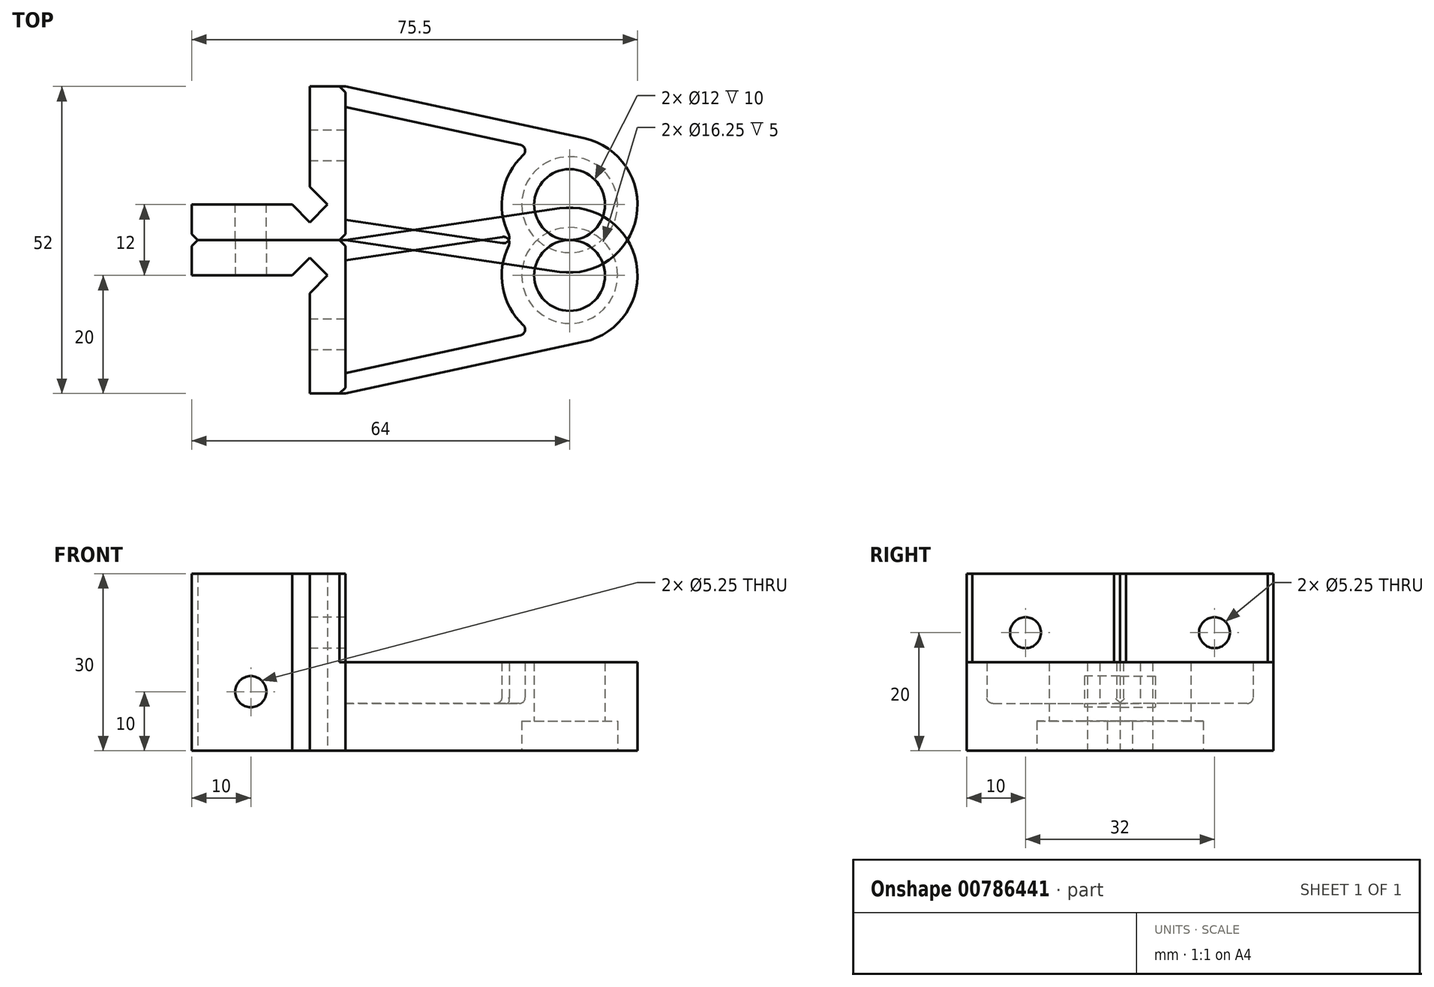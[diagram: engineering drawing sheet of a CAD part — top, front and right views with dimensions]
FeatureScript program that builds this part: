
annotation { "Feature Type Name" : "Feature", "Feature Type Description" : "" }
export const myFeature = defineFeature(function(context is Context, id is Id, definition is map)
    precondition{}
    {
        {
            var Q0;
            Q0=qCreatedBy(makeId("Top.planeOp"),FACE);
            var sketch = newSketch(context, id + "F0", { "sketchPlane" : qUnion([Q0])});
            skLineSegment(sketch, "E0", {"start": v(2.44, 11.24) * mm, "end": v(-38, 20) * mm, "construction": true});
            skLineSegment(sketch, "E1", {"start": v(-38, 20) * mm, "end": v(-44, 20) * mm, "construction": true});
            skLineSegment(sketch, "E2", {"start": v(-44, 20) * mm, "end": v(-44, 3) * mm, "construction": true});
            skLineSegment(sketch, "E3", {"start": v(-44, 3) * mm, "end": v(-41, 0) * mm, "construction": true});
            skLineSegment(sketch, "E4", {"start": v(-41, 0) * mm, "end": v(-44, -3) * mm, "construction": true});
            skLineSegment(sketch, "E5", {"start": v(-44, -3) * mm, "end": v(-47, 0) * mm, "construction": true});
            skLineSegment(sketch, "E6", {"start": v(-47, 0) * mm, "end": v(-64, 0) * mm, "construction": true});
            skLineSegment(sketch, "E7", {"start": v(-64, 0) * mm, "end": v(-64, -6) * mm, "construction": true});
            skLineSegment(sketch, "E8", {"start": v(-64, -6) * mm, "end": v(-38, -6) * mm, "construction": true});
            skLineSegment(sketch, "E9", {"start": v(-38, -6) * mm, "end": v(-1.68, -11.38) * mm, "construction": true});
            skCircle(sketch, "E10", {"center": v(0, 0) * mm, "radius": 6 * mm, "construction": true});
            skArc(sketch, "E11", {"start": v(2.44, 11.24) * mm, "mid": v(11.31, -2.06) * mm, "end": v(-1.68, -11.38) * mm, "construction": true});
            skLineSegment(sketch, "E12.0", {"start": v(1.72, 7.94) * mm, "end": v(-38, 16.55) * mm, "construction": true});
            skLineSegment(sketch, "E12.2", {"start": v(-38, -2.59) * mm, "end": v(-1.19, -8.04) * mm, "construction": true});
            skCircle(sketch, "E13.converted", {"center": v(0, 0) * mm, "radius": 8.12 * mm, "construction": true});
            skSolve(sketch);
        }
        {
            var Q0;
            Q0=qCreatedBy(makeId("Top.planeOp"),FACE);
            var sketch = newSketch(context, id + "F1", { "sketchPlane" : qUnion([Q0])});
            skLineSegment(sketch, "E14.0", {"start": v(2.44, 11.24) * mm, "end": v(-38, 20) * mm});
            skLineSegment(sketch, "E15.0", {"start": v(-38, -6) * mm, "end": v(-1.68, -11.38) * mm});
            skArc(sketch, "E16.0", {"start": v(2.44, 11.24) * mm, "mid": v(11.31, -2.06) * mm, "end": v(-1.68, -11.38) * mm});
            skCircle(sketch, "E17.0", {"center": v(0, 0) * mm, "radius": 6 * mm});
            skLineSegment(sketch, "E18", {"start": v(-38, 20) * mm, "end": v(-38, -6) * mm});
            skSolve(sketch);
        }
        {
            var Q0;
            Q0 = qSketchRegion(id + "F1", true);
            extrude(context, id + "F2", {"entities" : qUnion([Q0]), "depth" : 8 * mm, "offsetDistance" : 25 * mm});
        }
        {
            var Q0;
            Q0=qCreatedBy(makeId("Top.planeOp"),FACE);
            var sketch = newSketch(context, id + "F3", { "sketchPlane" : qUnion([Q0])});
            skLineSegment(sketch, "E19.0", {"start": v(-6.23, 9.66) * mm, "end": v(-38, 16.55) * mm});
            skLineSegment(sketch, "E20.0", {"start": v(-38, -2.59) * mm, "end": v(-9.24, -6.85) * mm});
            skLineSegment(sketch, "E21.0", {"start": v(2.44, 11.24) * mm, "end": v(-38, 20) * mm});
            skLineSegment(sketch, "E22.0", {"start": v(-38, -6) * mm, "end": v(-1.68, -11.38) * mm});
            skLineSegment(sketch, "E23", {"start": v(-38, 20) * mm, "end": v(-38, 16.55) * mm});
            skLineSegment(sketch, "E24", {"start": v(-38, -2.59) * mm, "end": v(-38, -6) * mm});
            skArc(sketch, "E25.converted", {"start": v(2.44, 11.24) * mm, "mid": v(11.31, -2.06) * mm, "end": v(-1.68, -11.38) * mm});
            skArc(sketch, "E26.trimOffspring", {"start": v(-9.24, -6.85) * mm, "mid": v(-11.31, 2.06) * mm, "end": v(-6.23, 9.66) * mm});
            skCircle(sketch, "E27.0", {"center": v(0, 0) * mm, "radius": 6 * mm});
            skSolve(sketch);
        }
        {
            var Q0;
            Q0 = qSketchRegion(id + "F3", true);
            extrude(context, id + "F4", {"entities" : qUnion([Q0]), "operationType" : NewBodyOperationType.ADD, "depth" : 15 * mm, "offsetDistance" : 25 * mm});
        }
        {
            var Q0;
            Q0=qCreatedBy(makeId("Top.planeOp"),FACE);
            var sketch = newSketch(context, id + "F5", { "sketchPlane" : qUnion([Q0])});
            skLineSegment(sketch, "E28.0", {"start": v(-38, 20) * mm, "end": v(-44, 20) * mm});
            skLineSegment(sketch, "E29.0", {"start": v(-44, 20) * mm, "end": v(-44, 3) * mm});
            skLineSegment(sketch, "E30.0", {"start": v(-44, 3) * mm, "end": v(-41, 0) * mm});
            skLineSegment(sketch, "E31.0", {"start": v(-41, 0) * mm, "end": v(-44, -3) * mm});
            skLineSegment(sketch, "E32.0", {"start": v(-44, -3) * mm, "end": v(-47, 0) * mm});
            skLineSegment(sketch, "E33.0", {"start": v(-47, 0) * mm, "end": v(-64, 0) * mm});
            skLineSegment(sketch, "E34.0", {"start": v(-64, 0) * mm, "end": v(-64, -6) * mm});
            skLineSegment(sketch, "E35.0", {"start": v(-64, -6) * mm, "end": v(-38, -6) * mm});
            skLineSegment(sketch, "E36", {"start": v(-38, 20) * mm, "end": v(-38, -6) * mm});
            skSolve(sketch);
        }
        {
            var Q0;
            Q0 = qSketchRegion(id + "F5", true);
            extrude(context, id + "F6", {"entities" : qUnion([Q0]), "operationType" : NewBodyOperationType.ADD, "depth" : 30 * mm, "offsetDistance" : 25 * mm});
        }
        {
            var Q0;
            Q0=makeQuery(id+"F6.opExtrude","SWEPT_EDGE",EDGE,{"disambiguationData":[OSD([sQuery(id+"F5.wireOp",EDGE,"E34.0"),sQuery(id+"F5.wireOp",EDGE,"E35.0")])]});
            var Q1;
            Q1=makeQuery(id+"F6.boolean.opBoolean","SPLIT",EDGE,{"derivedFrom":makeQuery(id+"F6.opExtrude","SWEPT_EDGE",EDGE,{"disambiguationData":[OSD([sQuery(id+"F5.wireOp",EDGE,"E28.0"),sQuery(id+"F5.wireOp",EDGE,"E36")])]})});
            var Q2;
            Q2=makeQuery(id+"F6.boolean.opBoolean","SPLIT",EDGE,{"derivedFrom":makeQuery(id+"F6.opExtrude","SWEPT_EDGE",EDGE,{"disambiguationData":[OSD([sQuery(id+"F5.wireOp",EDGE,"E35.0"),sQuery(id+"F5.wireOp",EDGE,"E36")])]})});
            chamfer(context, id + "F7", {"entities" : qUnion([Q0, Q1, Q2]), "width" : 1 * mm, "tangentPropagation" : true});
        }
        {
            var Q0;
            Q0=makeQuery(id+"F4.boolean.opBoolean","INTERSECT",EDGE,{"derivedFrom":[makeQuery(id+"F2.opExtrude","CAP_FACE",FACE,{"disambiguationData":[OSD([sQuery(id+"F1.wireOp",EDGE,"E14.0"),sQuery(id+"F1.wireOp",EDGE,"E15.0"),sQuery(id+"F1.wireOp",EDGE,"E16.0"),sQuery(id+"F1.wireOp",EDGE,"E17.0"),sQuery(id+"F1.wireOp",EDGE,"E18")])],"isStart":false}),makeQuery(id+"F4.opExtrude","SWEPT_FACE",FACE,{"disambiguationData":[OSD([sQuery(id+"F3.wireOp",EDGE,"E19.0")])]})]});
            var Q1;
            Q1=makeQuery(id+"F2.opExtrude","CAP_EDGE",EDGE,{"disambiguationData":[OSD([sQuery(id+"F1.wireOp",EDGE,"E18")])],"isStart":false});
            var Q2;
            Q2=makeQuery(id+"F4.opExtrude","CAP_EDGE",EDGE,{"disambiguationData":[OSD([sQuery(id+"F3.wireOp",EDGE,"E24")])],"isStart":false});
            var Q3;
            Q3=makeQuery(id+"F4.opExtrude","CAP_EDGE",EDGE,{"disambiguationData":[OSD([sQuery(id+"F3.wireOp",EDGE,"E23")])],"isStart":false});
            var Q4;
            Q4=makeQuery(id+"F4.boolean.opBoolean","INTERSECT",EDGE,{"derivedFrom":[makeQuery(id+"F2.opExtrude","CAP_FACE",FACE,{"disambiguationData":[OSD([sQuery(id+"F1.wireOp",EDGE,"E14.0"),sQuery(id+"F1.wireOp",EDGE,"E15.0"),sQuery(id+"F1.wireOp",EDGE,"E16.0"),sQuery(id+"F1.wireOp",EDGE,"E17.0"),sQuery(id+"F1.wireOp",EDGE,"E18")])],"isStart":false}),makeQuery(id+"F4.opExtrude","SWEPT_FACE",FACE,{"disambiguationData":[OSD([sQuery(id+"F3.wireOp",EDGE,"E26.trimOffspring")])]})]});
            var Q5;
            Q5=makeQuery(id+"F4.opExtrude","SWEPT_EDGE",EDGE,{"disambiguationData":[OSD([sQuery(id+"F3.wireOp",EDGE,"E19.0"),sQuery(id+"F3.wireOp",EDGE,"E26.trimOffspring")])]});
            var Q6;
            Q6=makeQuery(id+"F4.opExtrude","SWEPT_EDGE",EDGE,{"disambiguationData":[OSD([sQuery(id+"F3.wireOp",EDGE,"E20.0"),sQuery(id+"F3.wireOp",EDGE,"E26.trimOffspring")])]});
            var Q7;
            Q7=makeQuery(id+"F4.opExtrude","SWEPT_EDGE",EDGE,{"disambiguationData":[OSD([sQuery(id+"F3.wireOp",EDGE,"E19.0"),sQuery(id+"F3.wireOp",EDGE,"E23")])]});
            var Q8;
            Q8=makeQuery(id+"F4.opExtrude","SWEPT_EDGE",EDGE,{"disambiguationData":[OSD([sQuery(id+"F3.wireOp",EDGE,"E20.0"),sQuery(id+"F3.wireOp",EDGE,"E24")])]});
            fillet(context, id + "F8", {"entities" : qUnion([Q0, Q1, Q2, Q3, Q4, Q5, Q6, Q7, Q8]), "radius" : 1 * mm, "tangentPropagation" : true, "allowEdgeOverflow" : false});
        }
        {
            var Q0;
            Q0=makeQuery(id+"F6.boolean.opBoolean","MERGE",FACE,{"derivedFrom":[makeQuery(id+"F4.boolean.opBoolean","MERGE",FACE,{"derivedFrom":[makeQuery(id+"F2.opExtrude","CAP_FACE",FACE,{"disambiguationData":[OSD([sQuery(id+"F1.wireOp",EDGE,"E14.0"),sQuery(id+"F1.wireOp",EDGE,"E15.0"),sQuery(id+"F1.wireOp",EDGE,"E16.0"),sQuery(id+"F1.wireOp",EDGE,"E17.0"),sQuery(id+"F1.wireOp",EDGE,"E18")])],"isStart":true}),makeQuery(id+"F4.opExtrude","CAP_FACE",FACE,{"disambiguationData":[OSD([sQuery(id+"F3.wireOp",EDGE,"E19.0"),sQuery(id+"F3.wireOp",EDGE,"E20.0"),sQuery(id+"F3.wireOp",EDGE,"E21.0"),sQuery(id+"F3.wireOp",EDGE,"E22.0"),sQuery(id+"F3.wireOp",EDGE,"E23"),sQuery(id+"F3.wireOp",EDGE,"E24"),sQuery(id+"F3.wireOp",EDGE,"E25.converted"),sQuery(id+"F3.wireOp",EDGE,"E26.trimOffspring")])],"isStart":true})]}),makeQuery(id+"F6.opExtrude","CAP_FACE",FACE,{"disambiguationData":[OSD([sQuery(id+"F5.wireOp",EDGE,"E28.0"),sQuery(id+"F5.wireOp",EDGE,"E29.0"),sQuery(id+"F5.wireOp",EDGE,"E30.0"),sQuery(id+"F5.wireOp",EDGE,"E31.0"),sQuery(id+"F5.wireOp",EDGE,"E32.0"),sQuery(id+"F5.wireOp",EDGE,"E33.0"),sQuery(id+"F5.wireOp",EDGE,"E34.0"),sQuery(id+"F5.wireOp",EDGE,"E35.0"),sQuery(id+"F5.wireOp",EDGE,"E36")])],"isStart":true})]});
            var sketch = newSketch(context, id + "F9", { "sketchPlane" : qUnion([Q0])});
            skCircle(sketch, "E37.0", {"center": v(0, 0) * mm, "radius": 8.12 * mm});
            skSolve(sketch);
        }
        {
            var Q0;
            Q0 = qSketchRegion(id + "F9", true);
            extrude(context, id + "F10", {"entities" : qUnion([Q0]), "operationType" : NewBodyOperationType.REMOVE, "oppositeDirection" : true, "depth" : 5 * mm, "offsetDistance" : 25 * mm});
        }
        {
            var Q0;
            Q0=makeQuery(id+"F6.opExtrude","SWEPT_FACE",FACE,{"disambiguationData":[OSD([sQuery(id+"F5.wireOp",EDGE,"E33.0")])]});
            var sketch = newSketch(context, id + "F11", { "sketchPlane" : qUnion([Q0])});
            skCircle(sketch, "E38", {"center": v(54, 10) * mm, "radius": 2.62 * mm});
            skSolve(sketch);
        }
        {
            var Q0;
            Q0 = qSketchRegion(id + "F11", true);
            extrude(context, id + "F12", {"entities" : qUnion([Q0]), "operationType" : NewBodyOperationType.REMOVE, "endBound" : BoundingType.THROUGH_ALL, "oppositeDirection" : true, "depth" : 25 * mm, "offsetDistance" : 25 * mm});
        }
        {
            var Q0;
            Q0=makeQuery(id+"F6.opExtrude","SWEPT_FACE",FACE,{"disambiguationData":[OSD([sQuery(id+"F5.wireOp",EDGE,"E29.0")])]});
            var sketch = newSketch(context, id + "F13", { "sketchPlane" : qUnion([Q0])});
            skCircle(sketch, "E39", {"center": v(-10, 20) * mm, "radius": 2.62 * mm});
            skSolve(sketch);
        }
        {
            var Q0;
            Q0 = qSketchRegion(id + "F13", true);
            var Q1;
            Q1=makeQuery(id+"F6.opExtrude","SWEPT_FACE",FACE,{"disambiguationData":[OSD([sQuery(id+"F5.wireOp",EDGE,"E36")])]});
            extrude(context, id + "F14", {"entities" : qUnion([Q0]), "operationType" : NewBodyOperationType.REMOVE, "endBound" : BoundingType.UP_TO_SURFACE, "oppositeDirection" : true, "depth" : 25 * mm, "endBoundEntityFace" : qUnion([Q1]), "offsetDistance" : 25 * mm});
        }
        {
            var Q0;
            Q0=makeQuery(id+"F2.opExtrude","SWEPT_BODY",BODY,{"disambiguationData":[OSD([sQuery(id+"F1.wireOp",EDGE,"E14.0"),sQuery(id+"F1.wireOp",EDGE,"E15.0"),sQuery(id+"F1.wireOp",EDGE,"E16.0"),sQuery(id+"F1.wireOp",EDGE,"E17.0"),sQuery(id+"F1.wireOp",EDGE,"E18")])]});
            var Q1;
            Q1=makeQuery(id+"F6.opExtrude","SWEPT_FACE",FACE,{"disambiguationData":[OSD([sQuery(id+"F5.wireOp",EDGE,"E35.0")])]});
            mirror(context, id + "F15", {"entities" : qUnion([Q0]), "mirrorPlane" : qUnion([Q1])});
        }
    });
